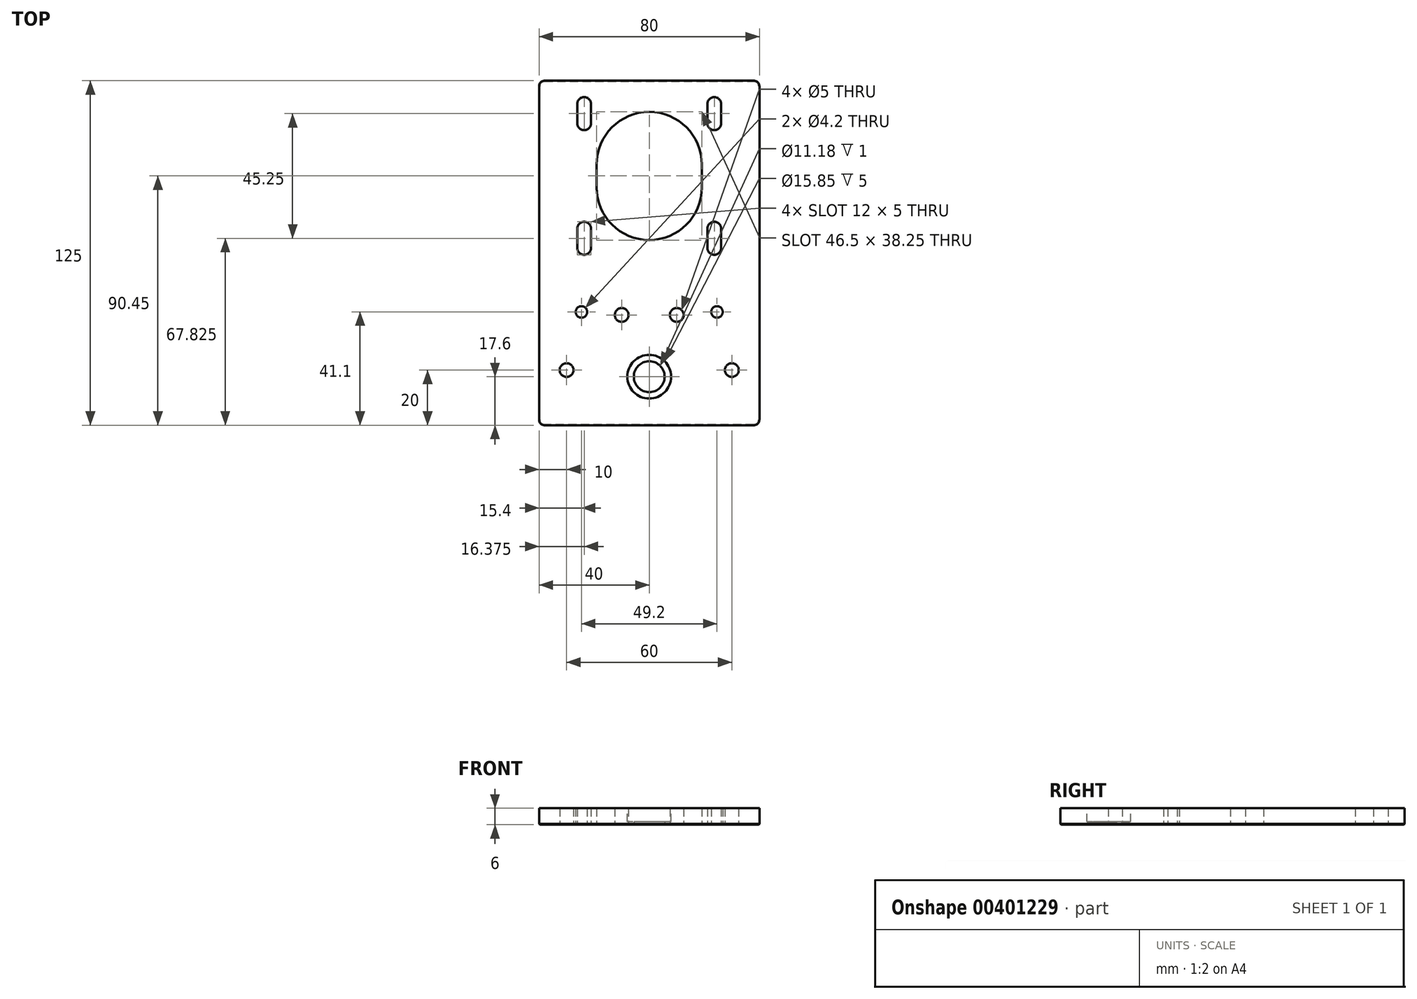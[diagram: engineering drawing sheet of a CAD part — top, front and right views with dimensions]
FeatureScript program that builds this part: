
annotation { "Feature Type Name" : "Feature", "Feature Type Description" : "" }
export const myFeature = defineFeature(function(context is Context, id is Id, definition is map)
    precondition{}
    {
        {
            var Q0;
            Q0=qCreatedBy(makeId("Top.planeOp"),FACE);
            var sketch = newSketch(context, id + "F0", { "sketchPlane" : qUnion([Q0])});
            skLineSegment(sketch, "E0.bottom", {"start": v(40, -20) * mm, "end": v(-40, -20) * mm});
            skLineSegment(sketch, "E0.top", {"start": v(40, 105) * mm, "end": v(-40, 105) * mm});
            skLineSegment(sketch, "E0.left", {"start": v(40, -20) * mm, "end": v(40, 105) * mm});
            skLineSegment(sketch, "E0.right", {"start": v(-40, -20) * mm, "end": v(-40, 105) * mm});
            skPoint(sketch, "E0.middle", {"position": v(0, 42.5) * mm});
            skCircle(sketch, "E1", {"center": v(30, 0) * mm, "radius": 2.5 * mm});
            skCircle(sketch, "E2", {"center": v(-30, 0) * mm, "radius": 2.5 * mm});
            skCircle(sketch, "E3", {"center": v(-10, 20) * mm, "radius": 2.5 * mm});
            skCircle(sketch, "E4", {"center": v(10, 20) * mm, "radius": 2.5 * mm});
            skLineSegment(sketch, "E5", {"start": v(-50.83, 20) * mm, "end": v(57.07, 20) * mm, "construction": true});
            skLineSegment(sketch, "E6", {"start": v(-45.44, 0) * mm, "end": v(50.07, 0) * mm, "construction": true});
            skLineSegment(sketch, "E7", {"start": v(0, -28.3) * mm, "end": v(0, 113.95) * mm, "construction": true});
            skArc(sketch, "E8", {"start": v(19.12, 74.58) * mm, "mid": v(0, 93.7) * mm, "end": v(-19.13, 74.58) * mm});
            skArc(sketch, "E9", {"start": v(-19.13, 66.33) * mm, "mid": v(0, 47.2) * mm, "end": v(19.12, 66.33) * mm});
            skLineSegment(sketch, "E10", {"start": v(-19.13, 74.58) * mm, "end": v(-19.13, 66.33) * mm});
            skLineSegment(sketch, "E11", {"start": v(19.12, 66.33) * mm, "end": v(19.12, 74.58) * mm});
            skPoint(sketch, "E12", {"position": v(0, 70.45) * mm});
            skLineSegment(sketch, "E13", {"start": v(-17.9, 70.45) * mm, "end": v(18.08, 70.45) * mm, "construction": true});
            skLineSegment(sketch, "E14", {"start": v(-37.18, 94.08) * mm, "end": v(36.45, 94.08) * mm, "construction": true});
            skLineSegment(sketch, "E15", {"start": v(-37.18, 46.83) * mm, "end": v(36.45, 46.83) * mm, "construction": true});
            skLineSegment(sketch, "E16", {"start": v(-23.63, 108.3) * mm, "end": v(-23.63, 32.5) * mm, "construction": true});
            skLineSegment(sketch, "E17", {"start": v(23.62, 106.17) * mm, "end": v(23.62, 32.38) * mm, "construction": true});
            skCircle(sketch, "E18", {"center": v(0, -2.4) * mm, "radius": 5.6 * mm});
            skLineSegment(sketch, "E19", {"start": v(-10.53, -2.4) * mm, "end": v(11.55, -2.4) * mm, "construction": true});
            skCircle(sketch, "E20", {"center": v(-24.6, 21.1) * mm, "radius": 2.1 * mm});
            skLineSegment(sketch, "E21", {"start": v(-28.3, 21.1) * mm, "end": v(18.3, 21.1) * mm, "construction": true});
            skCircle(sketch, "E22", {"center": v(24.6, 21.1) * mm, "radius": 2.1 * mm});
            skSolve(sketch);
        }
        {
            var Q0;
            Q0 = qSketchRegion(id + "F0", true);
            extrude(context, id + "F1", {"entities" : qUnion([Q0]), "depth" : 6 * mm});
        }
        {
            var Q0;
            Q0=qCreatedBy(makeId("Top.planeOp"),FACE);
            var sketch = newSketch(context, id + "F2", { "sketchPlane" : qUnion([Q0])});
            skArc(sketch, "E23", {"start": v(-21.13, 96.58) * mm, "mid": v(-23.63, 99.08) * mm, "end": v(-26.13, 96.58) * mm});
            skArc(sketch, "E24", {"start": v(-26.13, 89.58) * mm, "mid": v(-23.63, 87.08) * mm, "end": v(-21.13, 89.58) * mm});
            skArc(sketch, "E25", {"start": v(26.12, 96.58) * mm, "mid": v(23.62, 99.08) * mm, "end": v(21.12, 96.58) * mm});
            skArc(sketch, "E26", {"start": v(21.12, 89.58) * mm, "mid": v(23.62, 87.08) * mm, "end": v(26.12, 89.58) * mm});
            skLineSegment(sketch, "E27", {"start": v(-26.13, 96.58) * mm, "end": v(-26.13, 89.58) * mm});
            skLineSegment(sketch, "E28", {"start": v(-21.13, 96.58) * mm, "end": v(-21.13, 89.58) * mm});
            skLineSegment(sketch, "E29", {"start": v(26.12, 96.58) * mm, "end": v(26.12, 89.58) * mm});
            skLineSegment(sketch, "E30", {"start": v(21.12, 96.58) * mm, "end": v(21.12, 89.58) * mm});
            skArc(sketch, "E31.MirrorCS", {"start": v(26.12, 44.33) * mm, "mid": v(23.62, 41.83) * mm, "end": v(21.12, 44.32) * mm});
            skLineSegment(sketch, "E32.MirrorCS", {"start": v(21.12, 44.32) * mm, "end": v(21.12, 51.33) * mm});
            skLineSegment(sketch, "E33.MirrorCS", {"start": v(26.12, 44.33) * mm, "end": v(26.12, 51.33) * mm});
            skArc(sketch, "E34.MirrorCS", {"start": v(21.12, 51.33) * mm, "mid": v(23.62, 53.83) * mm, "end": v(26.12, 51.33) * mm});
            skArc(sketch, "E35.MirrorCS", {"start": v(-26.13, 51.32) * mm, "mid": v(-23.63, 53.82) * mm, "end": v(-21.13, 51.32) * mm});
            skLineSegment(sketch, "E36.MirrorCS", {"start": v(-26.13, 44.32) * mm, "end": v(-26.13, 51.32) * mm});
            skLineSegment(sketch, "E37.MirrorCS", {"start": v(-21.13, 44.32) * mm, "end": v(-21.13, 51.32) * mm});
            skArc(sketch, "E38.MirrorCS", {"start": v(-21.13, 44.32) * mm, "mid": v(-23.63, 41.82) * mm, "end": v(-26.13, 44.32) * mm});
            skSolve(sketch);
        }
        {
            var Q0;
            Q0 = qSketchRegion(id + "F2", true);
            extrude(context, id + "F3", {"entities" : qUnion([Q0]), "operationType" : NewBodyOperationType.REMOVE, "endBound" : BoundingType.UP_TO_NEXT, "depth" : 25 * mm});
        }
        {
            var Q0;
            Q0=makeQuery(id+"F1.opExtrude","SWEPT_EDGE",EDGE,{"disambiguationData":[OSD([sQuery(id+"F0.wireOp",EDGE,"E0.bottom"),sQuery(id+"F0.wireOp",EDGE,"E0.left")])]});
            var Q1;
            Q1=makeQuery(id+"F1.opExtrude","SWEPT_EDGE",EDGE,{"disambiguationData":[OSD([sQuery(id+"F0.wireOp",EDGE,"E0.bottom"),sQuery(id+"F0.wireOp",EDGE,"E0.right")])]});
            var Q2;
            Q2=makeQuery(id+"F1.opExtrude","SWEPT_EDGE",EDGE,{"disambiguationData":[OSD([sQuery(id+"F0.wireOp",EDGE,"E0.top"),sQuery(id+"F0.wireOp",EDGE,"E0.left")])]});
            var Q3;
            Q3=makeQuery(id+"F1.opExtrude","SWEPT_EDGE",EDGE,{"disambiguationData":[OSD([sQuery(id+"F0.wireOp",EDGE,"E0.top"),sQuery(id+"F0.wireOp",EDGE,"E0.right")])]});
            fillet(context, id + "F4", {"entities" : qUnion([Q0, Q1, Q2, Q3]), "radius" : 2 * mm, "tangentPropagation" : true, "allowEdgeOverflow" : false});
        }
        {
            var Q0;
            Q0=makeQuery(id+"F1.opExtrude","CAP_EDGE",EDGE,{"disambiguationData":[OSD([sQuery(id+"F0.wireOp",EDGE,"E0.right")])],"isStart":true});
            var Q1;
            {var subQ0=sQuery(id+"F0.wireOp",EDGE,"E0.right");var subQ1=sQuery(id+"F0.wireOp",EDGE,"E0.top");Q1=makeQuery(id+"F4.opFillet","BLEND_EDGE",EDGE,{"blendedFrom":[makeQuery(id+"F1.opExtrude","SWEPT_EDGE",EDGE,{"disambiguationData":[OSD([subQ1,subQ0])]}),makeQuery(id+"F1.opExtrude","CAP_FACE",FACE,{"disambiguationData":[OSD([sQuery(id+"F0.wireOp",EDGE,"E0.bottom"),subQ1,sQuery(id+"F0.wireOp",EDGE,"E0.left"),subQ0,sQuery(id+"F0.wireOp",EDGE,"E1"),sQuery(id+"F0.wireOp",EDGE,"E2"),sQuery(id+"F0.wireOp",EDGE,"E3"),sQuery(id+"F0.wireOp",EDGE,"E4"),sQuery(id+"F0.wireOp",EDGE,"E8"),sQuery(id+"F0.wireOp",EDGE,"E9"),sQuery(id+"F0.wireOp",EDGE,"E10"),sQuery(id+"F0.wireOp",EDGE,"E11"),sQuery(id+"F0.wireOp",EDGE,"E18")])],"isStart":true})],"blendedInto":[makeQuery(id+"F1.opExtrude","CAP_FACE",FACE,{"disambiguationData":[OSD([sQuery(id+"F0.wireOp",EDGE,"E0.bottom"),subQ1,sQuery(id+"F0.wireOp",EDGE,"E0.left"),subQ0,sQuery(id+"F0.wireOp",EDGE,"E1"),sQuery(id+"F0.wireOp",EDGE,"E2"),sQuery(id+"F0.wireOp",EDGE,"E3"),sQuery(id+"F0.wireOp",EDGE,"E4"),sQuery(id+"F0.wireOp",EDGE,"E8"),sQuery(id+"F0.wireOp",EDGE,"E9"),sQuery(id+"F0.wireOp",EDGE,"E10"),sQuery(id+"F0.wireOp",EDGE,"E11"),sQuery(id+"F0.wireOp",EDGE,"E18")])],"isStart":true})]});}
            var Q2;
            Q2=makeQuery(id+"F1.opExtrude","CAP_EDGE",EDGE,{"disambiguationData":[OSD([sQuery(id+"F0.wireOp",EDGE,"E0.top")])],"isStart":true});
            var Q3;
            {var subQ0=sQuery(id+"F0.wireOp",EDGE,"E0.left");var subQ1=sQuery(id+"F0.wireOp",EDGE,"E0.top");Q3=makeQuery(id+"F4.opFillet","BLEND_EDGE",EDGE,{"blendedFrom":[makeQuery(id+"F1.opExtrude","SWEPT_EDGE",EDGE,{"disambiguationData":[OSD([subQ1,subQ0])]}),makeQuery(id+"F1.opExtrude","CAP_FACE",FACE,{"disambiguationData":[OSD([sQuery(id+"F0.wireOp",EDGE,"E0.bottom"),subQ1,subQ0,sQuery(id+"F0.wireOp",EDGE,"E0.right"),sQuery(id+"F0.wireOp",EDGE,"E1"),sQuery(id+"F0.wireOp",EDGE,"E2"),sQuery(id+"F0.wireOp",EDGE,"E3"),sQuery(id+"F0.wireOp",EDGE,"E4"),sQuery(id+"F0.wireOp",EDGE,"E8"),sQuery(id+"F0.wireOp",EDGE,"E9"),sQuery(id+"F0.wireOp",EDGE,"E10"),sQuery(id+"F0.wireOp",EDGE,"E11"),sQuery(id+"F0.wireOp",EDGE,"E18")])],"isStart":true})],"blendedInto":[makeQuery(id+"F1.opExtrude","CAP_FACE",FACE,{"disambiguationData":[OSD([sQuery(id+"F0.wireOp",EDGE,"E0.bottom"),subQ1,subQ0,sQuery(id+"F0.wireOp",EDGE,"E0.right"),sQuery(id+"F0.wireOp",EDGE,"E1"),sQuery(id+"F0.wireOp",EDGE,"E2"),sQuery(id+"F0.wireOp",EDGE,"E3"),sQuery(id+"F0.wireOp",EDGE,"E4"),sQuery(id+"F0.wireOp",EDGE,"E8"),sQuery(id+"F0.wireOp",EDGE,"E9"),sQuery(id+"F0.wireOp",EDGE,"E10"),sQuery(id+"F0.wireOp",EDGE,"E11"),sQuery(id+"F0.wireOp",EDGE,"E18")])],"isStart":true})]});}
            var Q4;
            Q4=makeQuery(id+"F1.opExtrude","CAP_EDGE",EDGE,{"disambiguationData":[OSD([sQuery(id+"F0.wireOp",EDGE,"E0.left")])],"isStart":true});
            var Q5;
            {var subQ0=sQuery(id+"F0.wireOp",EDGE,"E0.left");var subQ1=sQuery(id+"F0.wireOp",EDGE,"E0.bottom");Q5=makeQuery(id+"F4.opFillet","BLEND_EDGE",EDGE,{"blendedFrom":[makeQuery(id+"F1.opExtrude","SWEPT_EDGE",EDGE,{"disambiguationData":[OSD([subQ1,subQ0])]}),makeQuery(id+"F1.opExtrude","CAP_FACE",FACE,{"disambiguationData":[OSD([subQ1,sQuery(id+"F0.wireOp",EDGE,"E0.top"),subQ0,sQuery(id+"F0.wireOp",EDGE,"E0.right"),sQuery(id+"F0.wireOp",EDGE,"E1"),sQuery(id+"F0.wireOp",EDGE,"E2"),sQuery(id+"F0.wireOp",EDGE,"E3"),sQuery(id+"F0.wireOp",EDGE,"E4"),sQuery(id+"F0.wireOp",EDGE,"E8"),sQuery(id+"F0.wireOp",EDGE,"E9"),sQuery(id+"F0.wireOp",EDGE,"E10"),sQuery(id+"F0.wireOp",EDGE,"E11"),sQuery(id+"F0.wireOp",EDGE,"E18")])],"isStart":true})],"blendedInto":[makeQuery(id+"F1.opExtrude","CAP_FACE",FACE,{"disambiguationData":[OSD([subQ1,sQuery(id+"F0.wireOp",EDGE,"E0.top"),subQ0,sQuery(id+"F0.wireOp",EDGE,"E0.right"),sQuery(id+"F0.wireOp",EDGE,"E1"),sQuery(id+"F0.wireOp",EDGE,"E2"),sQuery(id+"F0.wireOp",EDGE,"E3"),sQuery(id+"F0.wireOp",EDGE,"E4"),sQuery(id+"F0.wireOp",EDGE,"E8"),sQuery(id+"F0.wireOp",EDGE,"E9"),sQuery(id+"F0.wireOp",EDGE,"E10"),sQuery(id+"F0.wireOp",EDGE,"E11"),sQuery(id+"F0.wireOp",EDGE,"E18")])],"isStart":true})]});}
            var Q6;
            Q6=makeQuery(id+"F1.opExtrude","CAP_EDGE",EDGE,{"disambiguationData":[OSD([sQuery(id+"F0.wireOp",EDGE,"E0.bottom")])],"isStart":true});
            var Q7;
            {var subQ0=sQuery(id+"F0.wireOp",EDGE,"E0.right");var subQ1=sQuery(id+"F0.wireOp",EDGE,"E0.bottom");Q7=makeQuery(id+"F4.opFillet","BLEND_EDGE",EDGE,{"blendedFrom":[makeQuery(id+"F1.opExtrude","SWEPT_EDGE",EDGE,{"disambiguationData":[OSD([subQ1,subQ0])]}),makeQuery(id+"F1.opExtrude","CAP_FACE",FACE,{"disambiguationData":[OSD([subQ1,sQuery(id+"F0.wireOp",EDGE,"E0.top"),sQuery(id+"F0.wireOp",EDGE,"E0.left"),subQ0,sQuery(id+"F0.wireOp",EDGE,"E1"),sQuery(id+"F0.wireOp",EDGE,"E2"),sQuery(id+"F0.wireOp",EDGE,"E3"),sQuery(id+"F0.wireOp",EDGE,"E4"),sQuery(id+"F0.wireOp",EDGE,"E8"),sQuery(id+"F0.wireOp",EDGE,"E9"),sQuery(id+"F0.wireOp",EDGE,"E10"),sQuery(id+"F0.wireOp",EDGE,"E11"),sQuery(id+"F0.wireOp",EDGE,"E18")])],"isStart":true})],"blendedInto":[makeQuery(id+"F1.opExtrude","CAP_FACE",FACE,{"disambiguationData":[OSD([subQ1,sQuery(id+"F0.wireOp",EDGE,"E0.top"),sQuery(id+"F0.wireOp",EDGE,"E0.left"),subQ0,sQuery(id+"F0.wireOp",EDGE,"E1"),sQuery(id+"F0.wireOp",EDGE,"E2"),sQuery(id+"F0.wireOp",EDGE,"E3"),sQuery(id+"F0.wireOp",EDGE,"E4"),sQuery(id+"F0.wireOp",EDGE,"E8"),sQuery(id+"F0.wireOp",EDGE,"E9"),sQuery(id+"F0.wireOp",EDGE,"E10"),sQuery(id+"F0.wireOp",EDGE,"E11"),sQuery(id+"F0.wireOp",EDGE,"E18")])],"isStart":true})]});}
            chamfer(context, id + "F5", {"entities" : qUnion([Q0, Q1, Q2, Q3, Q4, Q5, Q6, Q7]), "width" : .25 * mm, "tangentPropagation" : true});
        }
        {
            var Q0;
            Q0=makeQuery(id+"F1.opExtrude","CAP_FACE",FACE,{"disambiguationData":[OSD([sQuery(id+"F0.wireOp",EDGE,"E0.bottom"),sQuery(id+"F0.wireOp",EDGE,"E0.top"),sQuery(id+"F0.wireOp",EDGE,"E0.left"),sQuery(id+"F0.wireOp",EDGE,"E0.right"),sQuery(id+"F0.wireOp",EDGE,"E1"),sQuery(id+"F0.wireOp",EDGE,"E2"),sQuery(id+"F0.wireOp",EDGE,"E3"),sQuery(id+"F0.wireOp",EDGE,"E4"),sQuery(id+"F0.wireOp",EDGE,"E8"),sQuery(id+"F0.wireOp",EDGE,"E9"),sQuery(id+"F0.wireOp",EDGE,"E10"),sQuery(id+"F0.wireOp",EDGE,"E11"),sQuery(id+"F0.wireOp",EDGE,"E18"),sQuery(id+"F0.wireOp",EDGE,"E20"),sQuery(id+"F0.wireOp",EDGE,"E22")])],"isStart":false});
            var sketch = newSketch(context, id + "F6", { "sketchPlane" : qUnion([Q0])});
            skCircle(sketch, "E39", {"center": v(0, -2.4) * mm, "radius": 7.92 * mm});
            skSolve(sketch);
        }
        {
            var Q0;
            Q0=makeQuery(id+"F6.imprint","IMPRINT",FACE,{"disambiguationData":[TD([[makeQuery(id+"F6.imprint","IMPRINT",EDGE,{"derivedFrom":sQuery(id+"F6.wireOp",EDGE,"E39")}),1.0]])]});
            extrude(context, id + "F7", {"entities" : qUnion([Q0]), "operationType" : NewBodyOperationType.REMOVE, "oppositeDirection" : true, "depth" : 5 * mm});
        }
    });
